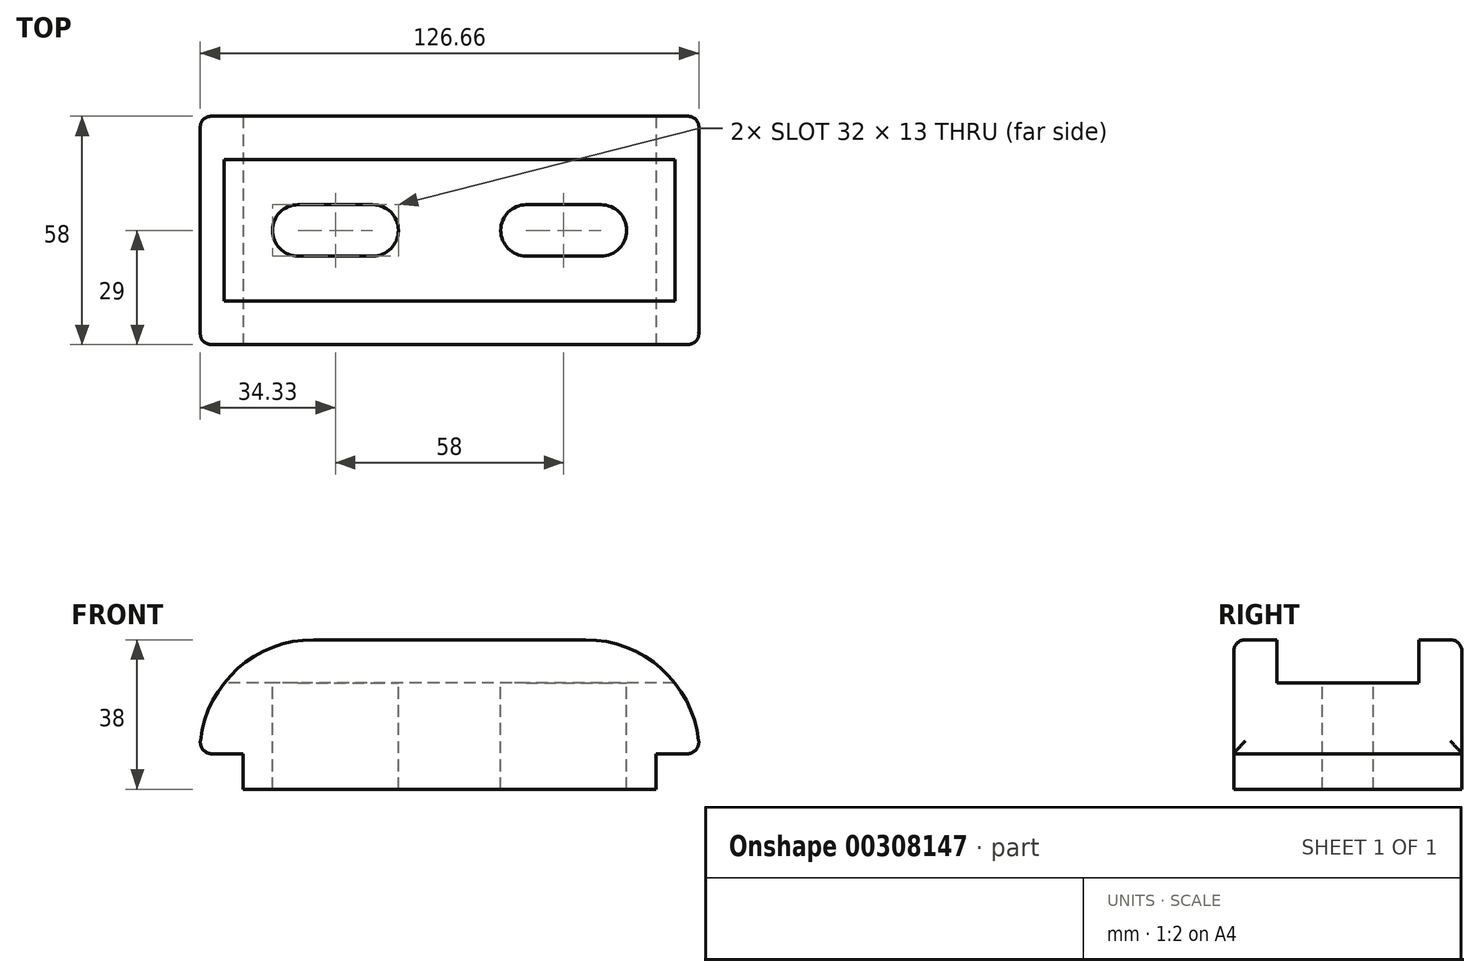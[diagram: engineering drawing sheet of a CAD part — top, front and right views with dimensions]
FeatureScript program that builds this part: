
annotation { "Feature Type Name" : "Feature", "Feature Type Description" : "" }
export const myFeature = defineFeature(function(context is Context, id is Id, definition is map)
    precondition{}
    {
        {
            var Q0;
            Q0=qCreatedBy(makeId("Front.planeOp"),FACE);
            var sketch = newSketch(context, id + "F0", { "sketchPlane" : qUnion([Q0])});
            skLineSegment(sketch, "E0", {"start": v(0, 0) * mm, "end": v(105, 0) * mm});
            skLineSegment(sketch, "E1", {"start": v(105, 0) * mm, "end": v(105, 9) * mm});
            skLineSegment(sketch, "E2", {"start": v(105, 9) * mm, "end": v(116, 9) * mm});
            skLineSegment(sketch, "E3", {"start": v(0, 0) * mm, "end": v(0, 9) * mm});
            skLineSegment(sketch, "E4", {"start": v(0, 9) * mm, "end": v(-11, 9) * mm});
            skLineSegment(sketch, "E5", {"start": v(-11, 9) * mm, "end": v(-11, 9) * mm});
            skLineSegment(sketch, "E6", {"start": v(18, 38) * mm, "end": v(87, 38) * mm});
            skLineSegment(sketch, "E7", {"start": v(116, 9) * mm, "end": v(116, 9) * mm});
            skPoint(sketch, "E8.visualSharp", {"position": v(-11, 38) * mm});
            skArc(sketch, "E8.filletArc", {"start": v(18, 38) * mm, "mid": v(-2.5, 29.5) * mm, "end": v(-11, 9) * mm});
            skPoint(sketch, "E9.visualSharp", {"position": v(116, 38) * mm});
            skArc(sketch, "E9.filletArc", {"start": v(116, 9) * mm, "mid": v(107.5, 29.5) * mm, "end": v(87, 38) * mm});
            skSolve(sketch);
        }
        {
            var Q0;
            Q0 = qSketchRegion(id + "F0", true);
            extrude(context, id + "F1", {"entities" : qUnion([Q0]), "oppositeDirection" : true, "depth" : 58 * mm});
        }
        {
            var Q0;
            Q0=qCreatedBy(makeId("Right.planeOp"),FACE);
            cPlane(context, id + "F2", {"entities" : qUnion([Q0]), "cplaneType" : CPlaneType.OFFSET, "offset" : 11 * mm, "oppositeDirection" : true, "width" : 150 * mm, "height" : 150 * mm});
        }
        {
            var Q0;
            Q0=qCreatedBy(id+"F2.planeOp",FACE);
            var sketch = newSketch(context, id + "F3", { "sketchPlane" : qUnion([Q0])});
            skLineSegment(sketch, "E10", {"start": v(47, 38) * mm, "end": v(47, 27) * mm});
            skLineSegment(sketch, "E11", {"start": v(47, 27) * mm, "end": v(11, 27) * mm});
            skLineSegment(sketch, "E12", {"start": v(11, 27) * mm, "end": v(11, 38) * mm});
            skLineSegment(sketch, "E13", {"start": v(11, 38) * mm, "end": v(47, 38) * mm});
            skSolve(sketch);
        }
        {
            var Q0;
            Q0 = qSketchRegion(id + "F3", true);
            extrude(context, id + "F4", {"entities" : qUnion([Q0]), "operationType" : NewBodyOperationType.REMOVE, "depth" : 127 * mm});
        }
        {
            var Q0;
            Q0=makeQuery(id+"F4.boolean.opBoolean","COPY",FACE,{"derivedFrom":makeQuery(id+"F4.opExtrude","SWEPT_FACE",FACE,{"disambiguationData":[OSD([sQuery(id+"F3.wireOp",EDGE,"E11")])]})});
            var sketch = newSketch(context, id + "F5", { "sketchPlane" : qUnion([Q0])});
            skArc(sketch, "E14", {"start": v(14, 35.5) * mm, "mid": v(7.5, 29) * mm, "end": v(14, 22.5) * mm});
            skArc(sketch, "E15", {"start": v(33, 22.5) * mm, "mid": v(39.5, 29) * mm, "end": v(33, 35.5) * mm});
            skLineSegment(sketch, "E16", {"start": v(14, 22.5) * mm, "end": v(33, 22.5) * mm});
            skLineSegment(sketch, "E17", {"start": v(33, 35.5) * mm, "end": v(14, 35.5) * mm});
            skArc(sketch, "E18", {"start": v(91, 22.5) * mm, "mid": v(97.5, 29) * mm, "end": v(91, 35.5) * mm});
            skArc(sketch, "E19", {"start": v(72, 35.5) * mm, "mid": v(65.5, 29) * mm, "end": v(72, 22.5) * mm});
            skLineSegment(sketch, "E20", {"start": v(72, 22.5) * mm, "end": v(91, 22.5) * mm});
            skLineSegment(sketch, "E21", {"start": v(91, 35.5) * mm, "end": v(72, 35.5) * mm});
            skSolve(sketch);
        }
        {
            var Q0;
            Q0 = qSketchRegion(id + "F5", true);
            extrude(context, id + "F6", {"entities" : qUnion([Q0]), "operationType" : NewBodyOperationType.REMOVE, "oppositeDirection" : true, "depth" : 38 * mm});
        }
        {
            var Q0;
            Q0=makeQuery(id+"F1.opExtrude","CAP_EDGE",EDGE,{"disambiguationData":[OSD([sQuery(id+"F0.wireOp",EDGE,"E9.filletArc")])],"isStart":true});
            var Q1;
            Q1=makeQuery(id+"F1.opExtrude","SWEPT_EDGE",EDGE,{"disambiguationData":[OSD([sQuery(id+"F0.wireOp",EDGE,"E2"),sQuery(id+"F0.wireOp",EDGE,"E9.filletArc")])]});
            var Q2;
            Q2=makeQuery(id+"F1.opExtrude","CAP_EDGE",EDGE,{"disambiguationData":[OSD([sQuery(id+"F0.wireOp",EDGE,"E9.filletArc")])],"isStart":false});
            var Q3;
            Q3=makeQuery(id+"F1.opExtrude","SWEPT_EDGE",EDGE,{"disambiguationData":[OSD([sQuery(id+"F0.wireOp",EDGE,"E4"),sQuery(id+"F0.wireOp",EDGE,"E8.filletArc")])]});
            fillet(context, id + "F7", {"entities" : qUnion([Q0, Q1, Q2, Q3]), "radius" : 3 * mm, "tangentPropagation" : true, "allowEdgeOverflow" : false});
        }
    });
